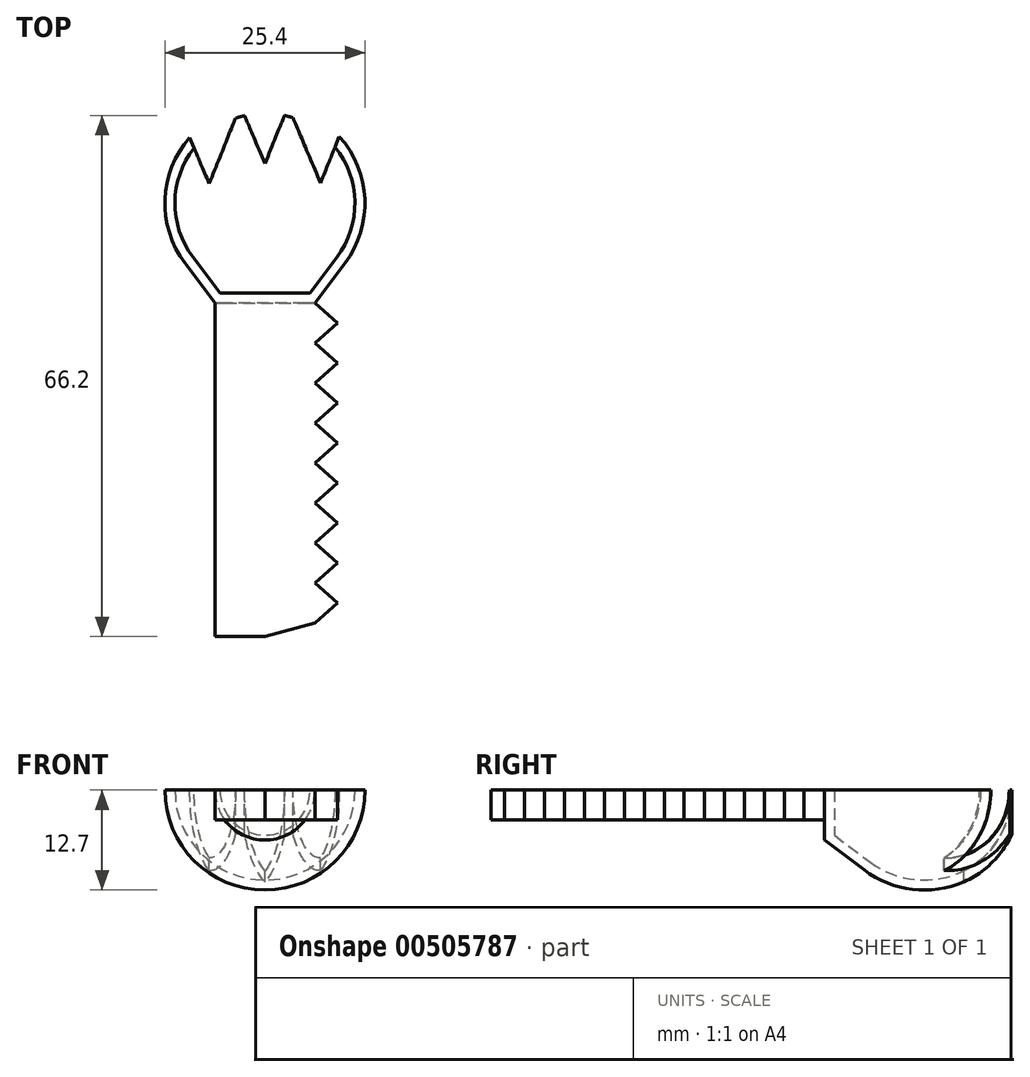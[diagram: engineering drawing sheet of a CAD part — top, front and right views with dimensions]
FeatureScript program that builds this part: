
annotation { "Feature Type Name" : "Feature", "Feature Type Description" : "" }
export const myFeature = defineFeature(function(context is Context, id is Id, definition is map)
    precondition{}
    {
        {
            var Q0;
            Q0=qCreatedBy(makeId("Top.planeOp"),FACE);
            var sketch = newSketch(context, id + "F0", { "sketchPlane" : qUnion([Q0])});
            skLineSegment(sketch, "E0", {"start": v(0, 0) * mm, "end": v(0, -42.34) * mm});
            skLineSegment(sketch, "E1", {"start": v(0, -42.34) * mm, "end": v(6.35, -40.64) * mm});
            skLineSegment(sketch, "E2", {"start": v(6.35, -40.64) * mm, "end": v(6.35, 0) * mm});
            skLineSegment(sketch, "E3", {"start": v(6.35, 0) * mm, "end": v(0, 0) * mm});
            skLineSegment(sketch, "E4", {"start": v(6.35, -40.64) * mm, "end": v(9.19, -38.1) * mm});
            skLineSegment(sketch, "E5", {"start": v(9.19, -38.1) * mm, "end": v(6.35, -35.56) * mm});
            skLineSegment(sketch, "E6", {"start": v(6.35, -35.56) * mm, "end": v(9.19, -33.02) * mm});
            skLineSegment(sketch, "E7", {"start": v(9.19, -33.02) * mm, "end": v(6.35, -30.48) * mm});
            skLineSegment(sketch, "E8", {"start": v(6.35, -30.48) * mm, "end": v(9.19, -27.94) * mm});
            skLineSegment(sketch, "E9", {"start": v(9.19, -27.94) * mm, "end": v(6.35, -25.4) * mm});
            skLineSegment(sketch, "E10", {"start": v(6.35, -25.4) * mm, "end": v(9.19, -22.86) * mm});
            skLineSegment(sketch, "E11", {"start": v(9.19, -22.86) * mm, "end": v(6.35, -20.32) * mm});
            skLineSegment(sketch, "E12", {"start": v(6.35, -20.32) * mm, "end": v(9.19, -17.78) * mm});
            skLineSegment(sketch, "E13", {"start": v(9.19, -17.78) * mm, "end": v(6.35, -15.24) * mm});
            skLineSegment(sketch, "E14", {"start": v(6.35, -15.24) * mm, "end": v(9.19, -12.7) * mm});
            skLineSegment(sketch, "E15", {"start": v(9.19, -12.7) * mm, "end": v(6.35, -10.16) * mm});
            skLineSegment(sketch, "E16", {"start": v(6.35, -10.16) * mm, "end": v(9.19, -7.62) * mm});
            skLineSegment(sketch, "E17", {"start": v(9.19, -7.62) * mm, "end": v(6.35, -5.08) * mm});
            skLineSegment(sketch, "E18", {"start": v(6.35, -5.08) * mm, "end": v(9.19, -2.54) * mm});
            skLineSegment(sketch, "E19", {"start": v(9.19, -2.54) * mm, "end": v(6.35, 0) * mm});
            skLineSegment(sketch, "E20", {"start": v(9.19, -2.54) * mm, "end": v(9.19, -38.1) * mm, "construction": true});
            skLineSegment(sketch, "E21", {"start": v(0, 0) * mm, "end": v(-6.35, 0) * mm});
            skLineSegment(sketch, "E22", {"start": v(-6.35, 0) * mm, "end": v(-6.35, -42.34) * mm});
            skLineSegment(sketch, "E23", {"start": v(-6.35, -42.34) * mm, "end": v(0, -42.34) * mm});
            skSolve(sketch);
        }
        {
            var Q0;
            {var subQ0=sQuery(id+"F0.wireOp",EDGE,"E6");Q0=makeQuery(id+"F0.imprint","IMPRINT",FACE,{"disambiguationData":[TD([[makeQuery(id+"F0.imprint","IMPRINT",EDGE,{"derivedFrom":subQ0}),1.0]])]});}
            var Q1;
            {var subQ0=sQuery(id+"F0.wireOp",EDGE,"E4");Q1=makeQuery(id+"F0.imprint","IMPRINT",FACE,{"disambiguationData":[TD([[makeQuery(id+"F0.imprint","IMPRINT",EDGE,{"derivedFrom":subQ0}),1.0]])]});}
            var Q2;
            {var subQ0=sQuery(id+"F0.wireOp",EDGE,"E8");Q2=makeQuery(id+"F0.imprint","IMPRINT",FACE,{"disambiguationData":[TD([[makeQuery(id+"F0.imprint","IMPRINT",EDGE,{"derivedFrom":subQ0}),1.0]])]});}
            var Q3;
            {var subQ0=sQuery(id+"F0.wireOp",EDGE,"E10");Q3=makeQuery(id+"F0.imprint","IMPRINT",FACE,{"disambiguationData":[TD([[makeQuery(id+"F0.imprint","IMPRINT",EDGE,{"derivedFrom":subQ0}),1.0]])]});}
            var Q4;
            {var subQ0=sQuery(id+"F0.wireOp",EDGE,"E12");Q4=makeQuery(id+"F0.imprint","IMPRINT",FACE,{"disambiguationData":[TD([[makeQuery(id+"F0.imprint","IMPRINT",EDGE,{"derivedFrom":subQ0}),1.0]])]});}
            var Q5;
            {var subQ0=sQuery(id+"F0.wireOp",EDGE,"E14");Q5=makeQuery(id+"F0.imprint","IMPRINT",FACE,{"disambiguationData":[TD([[makeQuery(id+"F0.imprint","IMPRINT",EDGE,{"derivedFrom":subQ0}),1.0]])]});}
            var Q6;
            {var subQ0=sQuery(id+"F0.wireOp",EDGE,"E16");Q6=makeQuery(id+"F0.imprint","IMPRINT",FACE,{"disambiguationData":[TD([[makeQuery(id+"F0.imprint","IMPRINT",EDGE,{"derivedFrom":subQ0}),1.0]])]});}
            var Q7;
            {var subQ2=sQuery(id+"F0.wireOp",EDGE,"E18");Q7=makeQuery(id+"F0.imprint","IMPRINT",FACE,{"disambiguationData":[TD([[makeQuery(id+"F0.imprint","IMPRINT",EDGE,{"derivedFrom":subQ2}),1.0]])]});}
            var Q8;
            Q8=makeQuery(id+"F0.imprint","IMPRINT",FACE,{"disambiguationData":[TD([[makeQuery(id+"F0.imprint","IMPRINT",EDGE,{"derivedFrom":sQuery(id+"F0.wireOp",EDGE,"E0")}),1.0]])]});
            var Q9;
            Q9=makeQuery(id+"F0.imprint","IMPRINT",FACE,{"disambiguationData":[TD([[makeQuery(id+"F0.imprint","IMPRINT",EDGE,{"derivedFrom":sQuery(id+"F0.wireOp",EDGE,"E0")}),-1.0]])]});
            extrude(context, id + "F1", {"entities" : qUnion([Q0, Q1, Q2, Q3, Q4, Q5, Q6, Q7, Q8, Q9]), "depth" : 3.8 * mm, "offsetDistance" : 25.4 * mm});
        }
        {
            var Q0;
            Q0=makeQuery(id+"F1.opExtrude","CAP_FACE",FACE,{"disambiguationData":[OSD([sQuery(id+"F0.wireOp",EDGE,"E0"),sQuery(id+"F0.wireOp",EDGE,"E1"),sQuery(id+"F0.wireOp",EDGE,"E3"),sQuery(id+"F0.wireOp",EDGE,"E4"),sQuery(id+"F0.wireOp",EDGE,"E5"),sQuery(id+"F0.wireOp",EDGE,"E6"),sQuery(id+"F0.wireOp",EDGE,"E7"),sQuery(id+"F0.wireOp",EDGE,"E8"),sQuery(id+"F0.wireOp",EDGE,"E9"),sQuery(id+"F0.wireOp",EDGE,"E10"),sQuery(id+"F0.wireOp",EDGE,"E11"),sQuery(id+"F0.wireOp",EDGE,"E12"),sQuery(id+"F0.wireOp",EDGE,"E13"),sQuery(id+"F0.wireOp",EDGE,"E14"),sQuery(id+"F0.wireOp",EDGE,"E15"),sQuery(id+"F0.wireOp",EDGE,"E16"),sQuery(id+"F0.wireOp",EDGE,"E17"),sQuery(id+"F0.wireOp",EDGE,"E18"),sQuery(id+"F0.wireOp",EDGE,"E19")])],"isStart":false});
            var sketch = newSketch(context, id + "F2", { "sketchPlane" : qUnion([Q0])});
            skLineSegment(sketch, "E24", {"start": v(0, 0) * mm, "end": v(0, 25.4) * mm});
            skArc(sketch, "E25", {"start": v(0, 0) * mm, "mid": v(12.7, 12.7) * mm, "end": v(0, 25.4) * mm});
            skLineSegment(sketch, "E26", {"start": v(0, 0) * mm, "end": v(6.35, 0) * mm});
            skLineSegment(sketch, "E27", {"start": v(6.35, 0) * mm, "end": v(10.16, 5.08) * mm});
            skSolve(sketch);
        }
        {
            var Q0;
            {var subQ0=sQuery(id+"F2.wireOp",EDGE,"E26");Q0=makeQuery(id+"F2.imprint","IMPRINT",FACE,{"disambiguationData":[TD([[makeQuery(id+"F2.imprint","IMPRINT",EDGE,{"derivedFrom":subQ0}),-1.0]])]});}
            var Q1;
            {var subQ0=sQuery(id+"F2.wireOp",EDGE,"E24");Q1=makeQuery(id+"F2.imprint","IMPRINT",FACE,{"disambiguationData":[TD([[makeQuery(id+"F2.imprint","IMPRINT",EDGE,{"derivedFrom":subQ0}),-1.0]])]});}
            var Q2;
            Q2=sQuery(id+"F2.wireOp",EDGE,"E24");
            revolve(context, id + "F3", {"entities" : qUnion([Q0, Q1]), "axis" : qUnion([Q2]), "revolveType" : RevolveType.ONE_DIRECTION, "angle" : 180 * degree});
        }
        {
            var Q0;
            Q0=makeQuery(id+"F3.opRevolve","CAP_FACE",FACE,{"disambiguationData":[OSD([sQuery(id+"F2.wireOp",EDGE,"E24"),sQuery(id+"F2.wireOp",EDGE,"E25"),sQuery(id+"F2.wireOp",EDGE,"E26"),sQuery(id+"F2.wireOp",EDGE,"E27")])],"isStart":true});
            shell(context, id + "F4", {"entities" : qUnion([Q0]), "thickness" : 1.27 * mm});
        }
        {
            var Q0;
            Q0=makeQuery(id+"F1.opExtrude","SWEPT_BODY",BODY,{"disambiguationData":[OSD([sQuery(id+"F0.wireOp",EDGE,"E0"),sQuery(id+"F0.wireOp",EDGE,"E1"),sQuery(id+"F0.wireOp",EDGE,"E3"),sQuery(id+"F0.wireOp",EDGE,"E4"),sQuery(id+"F0.wireOp",EDGE,"E5"),sQuery(id+"F0.wireOp",EDGE,"E6"),sQuery(id+"F0.wireOp",EDGE,"E7"),sQuery(id+"F0.wireOp",EDGE,"E8"),sQuery(id+"F0.wireOp",EDGE,"E9"),sQuery(id+"F0.wireOp",EDGE,"E10"),sQuery(id+"F0.wireOp",EDGE,"E11"),sQuery(id+"F0.wireOp",EDGE,"E12"),sQuery(id+"F0.wireOp",EDGE,"E13"),sQuery(id+"F0.wireOp",EDGE,"E14"),sQuery(id+"F0.wireOp",EDGE,"E15"),sQuery(id+"F0.wireOp",EDGE,"E16"),sQuery(id+"F0.wireOp",EDGE,"E17"),sQuery(id+"F0.wireOp",EDGE,"E18"),sQuery(id+"F0.wireOp",EDGE,"E19")])]});
            var Q1;
            Q1=makeQuery(id+"F3.opRevolve","SWEPT_BODY",BODY,{"disambiguationData":[OSD([sQuery(id+"F2.wireOp",EDGE,"E24"),sQuery(id+"F2.wireOp",EDGE,"E25"),sQuery(id+"F2.wireOp",EDGE,"E26"),sQuery(id+"F2.wireOp",EDGE,"E27")])]});
            booleanBodies(context, id + "F5", {"operationType" : BooleanOperationType.UNION, "tools" : qUnion([Q0, Q1])});
        }
        {
            var Q0;
            Q0=makeQuery(id+"F5.opBoolean","MERGE",FACE,{"derivedFrom":[makeQuery(id+"F1.opExtrude","CAP_FACE",FACE,{"disambiguationData":[OSD([sQuery(id+"F0.wireOp",EDGE,"E1"),sQuery(id+"F0.wireOp",EDGE,"E3"),sQuery(id+"F0.wireOp",EDGE,"E4"),sQuery(id+"F0.wireOp",EDGE,"E5"),sQuery(id+"F0.wireOp",EDGE,"E6"),sQuery(id+"F0.wireOp",EDGE,"E7"),sQuery(id+"F0.wireOp",EDGE,"E8"),sQuery(id+"F0.wireOp",EDGE,"E9"),sQuery(id+"F0.wireOp",EDGE,"E10"),sQuery(id+"F0.wireOp",EDGE,"E11"),sQuery(id+"F0.wireOp",EDGE,"E12"),sQuery(id+"F0.wireOp",EDGE,"E13"),sQuery(id+"F0.wireOp",EDGE,"E14"),sQuery(id+"F0.wireOp",EDGE,"E15"),sQuery(id+"F0.wireOp",EDGE,"E16"),sQuery(id+"F0.wireOp",EDGE,"E17"),sQuery(id+"F0.wireOp",EDGE,"E18"),sQuery(id+"F0.wireOp",EDGE,"E19"),sQuery(id+"F0.wireOp",EDGE,"E21"),sQuery(id+"F0.wireOp",EDGE,"E22"),sQuery(id+"F0.wireOp",EDGE,"E23")])],"isStart":false}),makeQuery(id+"F3.opRevolve","CAP_FACE",FACE,{"disambiguationData":[OSD([sQuery(id+"F2.wireOp",EDGE,"E24"),sQuery(id+"F2.wireOp",EDGE,"E25"),sQuery(id+"F2.wireOp",EDGE,"E26"),sQuery(id+"F2.wireOp",EDGE,"E27")])],"isStart":true})]});
            var sketch = newSketch(context, id + "F6", { "sketchPlane" : qUnion([Q0])});
            skLineSegment(sketch, "E28", {"start": v(9.45, 21.19) * mm, "end": v(7.07, 15.3) * mm});
            skLineSegment(sketch, "E29", {"start": v(7.07, 15.3) * mm, "end": v(2.94, 25.02) * mm});
            skLineSegment(sketch, "E30", {"start": v(2.94, 25.02) * mm, "end": v(0, 17.74) * mm});
            skLineSegment(sketch, "E31", {"start": v(0, 17.74) * mm, "end": v(-3.1, 25.06) * mm});
            skLineSegment(sketch, "E32", {"start": v(-3.1, 25.06) * mm, "end": v(-7.08, 15.21) * mm});
            skLineSegment(sketch, "E33", {"start": v(-7.08, 15.21) * mm, "end": v(-9.56, 21.06) * mm});
            skSolve(sketch);
        }
        {
            var Q0;
            {var subQ0=sQuery(id+"F6.wireOp",EDGE,"E33");var subQ1=sQuery(id+"F6.wireOp",EDGE,"E32");var subQ2=makeQuery(id+"F6.imprint","INTERSECT",VERTEX,{"derivedFrom":[subQ1,subQ0]});Q0=makeQuery(id+"F6.imprint","IMPRINT",FACE,{"disambiguationData":[TD([[makeQuery(id+"F6.imprint","IMPRINT",EDGE,{"disambiguationData":[TD([[subQ2,1.0]])],"derivedFrom":subQ1}),-1.0]])]});}
            var Q1;
            {var subQ0=sQuery(id+"F6.wireOp",EDGE,"E31");var subQ1=sQuery(id+"F6.wireOp",EDGE,"E30");var subQ2=makeQuery(id+"F6.imprint","INTERSECT",VERTEX,{"derivedFrom":[subQ1,subQ0]});Q1=makeQuery(id+"F6.imprint","IMPRINT",FACE,{"disambiguationData":[TD([[makeQuery(id+"F6.imprint","IMPRINT",EDGE,{"disambiguationData":[TD([[subQ2,1.0]])],"derivedFrom":subQ1}),-1.0]])]});}
            var Q2;
            {var subQ0=sQuery(id+"F6.wireOp",EDGE,"E29");var subQ1=sQuery(id+"F6.wireOp",EDGE,"E28");var subQ2=makeQuery(id+"F6.imprint","INTERSECT",VERTEX,{"derivedFrom":[subQ1,subQ0]});Q2=makeQuery(id+"F6.imprint","IMPRINT",FACE,{"disambiguationData":[TD([[makeQuery(id+"F6.imprint","IMPRINT",EDGE,{"disambiguationData":[TD([[subQ2,1.0]])],"derivedFrom":subQ1}),-1.0]])]});}
            var Q3;
            {var subQ1=sQuery(id+"F2.wireOp",EDGE,"E25");var subQ2=makeQuery(id+"F3.opRevolve","CAP_EDGE",EDGE,{"disambiguationData":[OSD([subQ1])],"isStart":true});var subQ6=sQuery(id+"F6.wireOp",EDGE,"E28");var subQ7=makeQuery(id+"F6.imprint","INTERSECT",VERTEX,{"derivedFrom":[subQ2,subQ6]});Q3=makeQuery(id+"F6.imprint","IMPRINT",FACE,{"disambiguationData":[TD([[makeQuery(id+"F6.imprint","IMPRINT",EDGE,{"disambiguationData":[TD([[subQ7,-1.0]])],"derivedFrom":subQ6}),-1.0]])]});}
            var Q4;
            {var subQ0=sQuery(id+"F6.wireOp",EDGE,"E30");var subQ1=sQuery(id+"F6.wireOp",EDGE,"E29");var subQ2=makeQuery(id+"F6.imprint","INTERSECT",VERTEX,{"derivedFrom":[subQ1,subQ0]});Q4=makeQuery(id+"F6.imprint","IMPRINT",FACE,{"disambiguationData":[TD([[makeQuery(id+"F6.imprint","IMPRINT",EDGE,{"disambiguationData":[TD([[subQ2,1.0]])],"derivedFrom":subQ1}),1.0]])]});}
            var Q5;
            {var subQ0=sQuery(id+"F6.wireOp",EDGE,"E31");var subQ1=sQuery(id+"F2.wireOp",EDGE,"E25");var subQ2=makeQuery(id+"F3.opRevolve","CAP_EDGE",EDGE,{"disambiguationData":[OSD([subQ1])],"isStart":true});var subQ3=makeQuery(id+"F6.imprint","INTERSECT",VERTEX,{"derivedFrom":[subQ2,subQ0]});Q5=makeQuery(id+"F6.imprint","IMPRINT",FACE,{"disambiguationData":[TD([[makeQuery(id+"F6.imprint","IMPRINT",EDGE,{"disambiguationData":[TD([[subQ3,1.0]])],"derivedFrom":subQ0}),1.0]])]});}
            var Q6;
            {var subQ0=sQuery(id+"F6.wireOp",EDGE,"E32");var subQ1=sQuery(id+"F2.wireOp",EDGE,"E25");var subQ2=makeQuery(id+"F3.opRevolve","CAP_EDGE",EDGE,{"disambiguationData":[OSD([subQ1])],"isStart":true});var subQ3=makeQuery(id+"F6.imprint","INTERSECT",VERTEX,{"derivedFrom":[subQ2,subQ0]});Q6=makeQuery(id+"F6.imprint","IMPRINT",FACE,{"disambiguationData":[TD([[makeQuery(id+"F6.imprint","IMPRINT",EDGE,{"disambiguationData":[TD([[subQ3,-1.0]])],"derivedFrom":subQ0}),-1.0]])]});}
            extrude(context, id + "F7", {"entities" : qUnion([Q0, Q1, Q2, Q3, Q4, Q5, Q6]), "operationType" : NewBodyOperationType.REMOVE, "oppositeDirection" : true, "depth" : 25.4 * mm, "offsetDistance" : 25.4 * mm});
        }
    });
